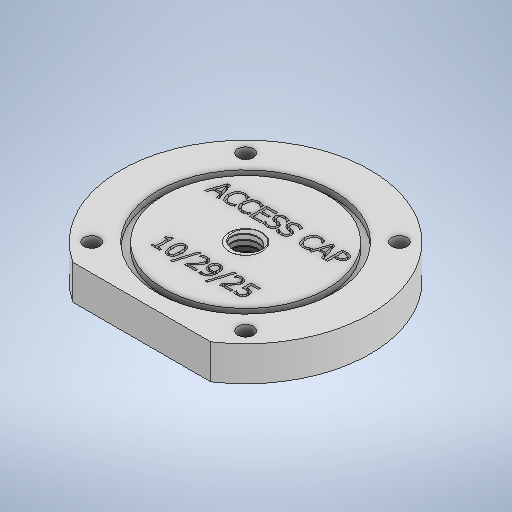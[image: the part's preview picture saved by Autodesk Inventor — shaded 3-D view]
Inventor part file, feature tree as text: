
AUTODESK INVENTOR PART (.ipt)
format: ipt  version: 2025 (Build 290162000, 162)  size: 1,171,968 bytes
history: native  units: mm
features: sketch x7, hole x2, extrude x1, pattern_circular x1, other x1, thread x1, revolve x1, helix x1, emboss x1
ambient origin geometry x8: Origin, YZ Plane, XZ Plane, XY Plane, X Axis, Y Axis, Z Axis, Center Point
bodies: Solid1 (feature_tree), Solid5 (feature_tree)
feature tree (16):
  extrude  "Base"  Depth=30.0mm
  hole  "Mounting Holes"  [1 undecoded]
  pattern_circular  "Circular Pattern1"  Count=4 Angle=360.0deg
  other  "Seal Groove"
  hole  "Wire Passthrough"  [1 undecoded]
  thread  "Thread3"  [1 undecoded]
  revolve  "Revolution5"  [1 undecoded]
  helix  "Coil4"  [1 undecoded]
  emboss  "Emboss1"
  sketch  "Sketch1"  dims[d0=72.0mm d1=30.0mm]
  sketch  "Sketch2"  dims[d2=10.0mm d3=0.0mm]
  sketch  "Sketch3"  dims[d4=4.5mm d5=6.0mm d6=8.0mm d7=4.0mm d8=90.0deg d9=8.0mm d10=20.594885mm d11=62.8mm]
  sketch  "Sketch4"  dims[d12=45.0deg d13=40.0mm d14=360.0deg]
  sketch  "Sketch13"  dims[d16=2.0mm d17=1.8mm d18=23.5mm]
  sketch  "Sketch14"  dims[d19=90.0deg]
  sketch  "Sketch15"  dims[d20=9.5mm d21=20.0mm d22=8.0mm d23=4.0mm d24=90.0deg d25=8.0mm d26=20.594885mm d36=9.599311mm d54=9.599311mm d74=9.599311mm d85=10.0mm d86=0.0mm d87=9.599311mm d88=0.240125mm d89=0.240125mm d92=1.5mm d94=9.599311mm d96=0.0mm d97=1.5015mm d98=13.0mm d99=10.0mm d100=0.0mm d101=0.0mm d102=0.0mm d103=0.0mm d104=0.0mm d105=1.0mm d106=0.0mm]
note: 5 required parameter values undecoded (feature->parameter linkage not recoverable at this tier; creation-order binding heuristic only, values carry confidence <= 0.55)